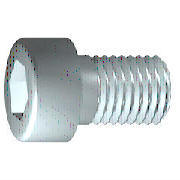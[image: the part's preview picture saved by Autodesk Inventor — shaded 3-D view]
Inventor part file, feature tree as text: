
AUTODESK INVENTOR PART (.ipt)
format: ipt  version: 2013 (Build 170138000, 138)  size: 180,736 bytes
history: native  units: mm (DEFAULTED — no unit token found)
features: sketch x2, extrude x1, plane x1, fillet x1
ambient origin geometry x7: Origin, YZ Plane, XY Plane, X Axis, Y Axis, Z Axis, Center Point
bodies: Solid1 (feature_tree), Body (feature_tree)
feature tree (5):
  extrude  "Slot"  Depth=0.306825mm
  plane  "Work Plane1"
  fillet  "Fillet2"  Radius=3.0mm
  sketch  "Sketch1"  dims[d1=18.0mm d2=0.306825mm d3=3.0mm]
  sketch  "Sketch2"  dims[d4=1.5mm d5=60.0deg d6=3.0mm d7=3.0mm d8=2.886751mm d9=5.5mm d10=90.0deg d11=10.0mm d12=0.0mm d13=18.0mm d14=0.0mm d15=0.306725mm d16=0.306725mm d17=0.3mm d19=0.0mm d26=35.0mm d27=45.0deg d28=0.0mm d29=0.0mm d30=0.1mm]
